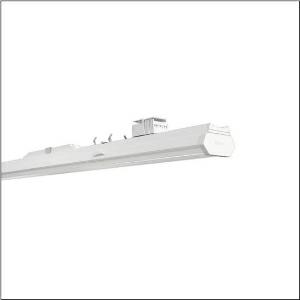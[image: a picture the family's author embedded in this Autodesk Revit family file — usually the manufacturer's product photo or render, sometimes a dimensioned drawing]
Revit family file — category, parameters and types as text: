
# Revit family: licross_21_protected_ho_52td12dn4e5m3s4
name_source: partatom
category: Lighting Fixtures
units: mm (PartAtom-declared; Revit-internal decimal feet)

## family parameters
Cut with Voids When Loaded = No
Host = Face
Light Source = No
Part Type = Normal
Room Calculation Point = No
Round Connector Dimension = Use Diameter
Shared = No

## types (1)
- --- (1 x LED, 910 lm, 7.6 W, 4000K)
    Apparent Load = 8 VA
    CIE Flux Codes = 70 91 97 98 100
    Color Rendering = 80
    Color Temperature = 4000K
    Default Elevation = 1800 mm
    Description = Licross 21 Protected HO, luminaire insert, of sheet steel, galvanised, coil coated, white, length: 1.500mm, width: 90mm, height: 103mm, LED rated luminous flux: 14.690lm, light colour: 840, SDCM (Standard Deviation of Colour Matching)MacAdam ≤ 3 SDCM (initial), control gear: DALI 2, with plug, 6-pole, with phase selection, for trunking rail, 9 or 11-core, mains connection: 220..240V, AC, 50/60Hz, rated input power: 89W, for trunking rail, 9-/11-core, internal wiring halogen-free, for emergency light function, converter,control gear: single battery element, battery: LiFePO4, 9Ah, primary light control with lens, of plastic, primary optical cover: cover, of PMMA, light emission: direct distribution, primary light characteristic: symmetric, protection rating (complete): IP54, insulation class (complete): insulation class I (protective earthing), certification: CE, UKCA, protection symbol: D if used in an environment with non-conductive dust loads with corresponding accessories, impact resistance: IK06, permissible ambient temperature for indoor applications: +5..+30°C, standard: EN 60598-2-22, LABS conformity tested according to VDMA 24364:2018-05, reducing of maximum allowable ambient temperature of 5°C with ceiling mounting, corresponds to IFS (International Featured Standards) requirements for safety and quality in the food industry, The light source and the operating device comply with the requirements of the Ecodesign Regulation (EU) 2019/2020 and are replaceable in accordance with this regulation, packaging unit: 1 piece
    Height = 92 mm
    Lamp = 1 x LED
    Lamp Light Flux = 910 lm
    Lamp Power = 7.6 W
    Lamp count = 1
    Length = 1500 mm
    Luminous efficacy = 120 lm/W
    Manufacturer = Siteco
    ModVariant = No
    Model = 52TD12DN4E5M3S4
    Mounting Place = Ceiling
    Mounting Type = Pendant
    Number of Poles = 1
    OnlyDefault = Yes
    Power Factor = 1
    Product Name = Licross 21 Protected HO
    Product group = luminaire insert | ceiling pendant
    ProductGroupID = 901
    Protection Class = Protection class I
    Protection Degree = IP 54
    RLX_Detail_Level = 1
    RLX_Emergency_Light_Flux = 0 lm
    RLX_Emergency_Type = 0
    RLX_Emergency_Type_DB = No
    RlxData = <blob elided: 25133 chars, md5=08877838>
    Socket = socket
    Standby Power = 0 W
    System Light Flux = 910 lm
    System Power = 8 W
    Type Comments = : emergency light operation: 3 h
    Type Image = l_1256148.jpg
    URL = http://relux.com
    VarID = @adj_111171
    Voltage = 0 V
    Weight = 0.00 kg
    Width = 88 mm

## geometry (parser evidence)
native form markers: Blend x4, Sweep x11
no freeform markers — native parametric forms only
